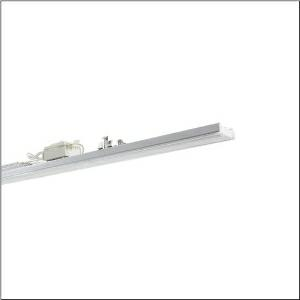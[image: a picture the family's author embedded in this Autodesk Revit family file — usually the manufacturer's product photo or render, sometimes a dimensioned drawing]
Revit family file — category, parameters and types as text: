
# Revit family: licross_r__21_recessed_mo_52te11dn4axg_b56d
name_source: partatom
category: Lighting Fixtures
units: mm (PartAtom-declared; Revit-internal decimal feet)

## family parameters
Cut with Voids When Loaded = No
Host = Face
Light Source = No
Part Type = Normal
Room Calculation Point = No
Round Connector Dimension = Use Diameter
Shared = No

## types (1)
- --- (1 x LED, 10120 lm, 58 W, 4000K)
    Apparent Load = 58 VA
    CIE Flux Codes = 89 96 99 100 100
    Color Rendering = 80
    Color Temperature = 4000K
    Default Elevation = 1800 mm
    Description = Licross® 21 Recessed MO, luminaire insert, of sheet steel, galvanised, coil coated, white, length: 1.500mm, width: 66mm, height: 67mm, LED rated luminous flux: 10.120lm, light colour: 840, control gear: DALI 2, with plug, 5-pole, with phase selection, mains connection: 220..240V, AC, 50/60Hz, rated input power: 58W, halogen-free wiring, primary light control with lens, of plastic, primary optical cover: cover, of PMMA, light emission: direct distribution, primary light characteristic: symmetric, protection rating (complete): IP54, insulation class (complete): insulation class I (protective earthing), certification: CE, ENEC, VDE, UKCA, protection symbol: D if used in an environment with non-conductive dust loads with corresponding accessories, impact resistance: IK06, permissible ambient temperature for indoor applications: -25..+35°C, corresponds to IFS (International Featured Standards) requirements for safety and quality in the food industry, reducing of maximum allowable ambient temperature of 5°C with ceiling mounting, LABS conformity tested according to VDMA 24364:2018-05, packaging unit: 1 piece
    Height = 58 mm
    Lamp = 1 x LED
    Lamp Light Flux = 10120 lm
    Lamp Power = 58 W
    Lamp count = 1
    Length = 1500 mm
    Luminous efficacy = 174 lm/W
    Manufacturer = Siteco
    ModVariant = No
    Model = 52TE11DN4AXG
    Mounting Place = Ceiling
    Mounting Type = Pendant
    Number of Poles = 1
    OnlyDefault = Yes
    Power Factor = 1
    Product Name = Licross® 21 Recessed MO
    Product group = luminaire insert
    ProductGroupID = 902
    Protection Class = Protection class I
    Protection Degree = IP 54
    RLX_Detail_Level = 1
    RLX_Emergency_Light_Flux = 0 lm
    RLX_Emergency_Type = 0
    RLX_Emergency_Type_DB = No
    RlxData = <blob elided: 24493 chars, md5=fceb64ea>
    Socket = socket
    Standby Power = 0 W
    System Light Flux = 10120 lm
    System Power = 58 W
    Type Comments = factory setting: luminous flux: 100 % | dim-lin: 254 | 390 mA
    Type Image = l_1296930.jpg
    URL = http://relux.com
    VarID = @adj_126806
    Voltage = 0 V
    Weight = 0.00 kg
    Width = 66 mm

## geometry (parser evidence)
native form markers: Blend x4, Sweep x10
no freeform markers — native parametric forms only
